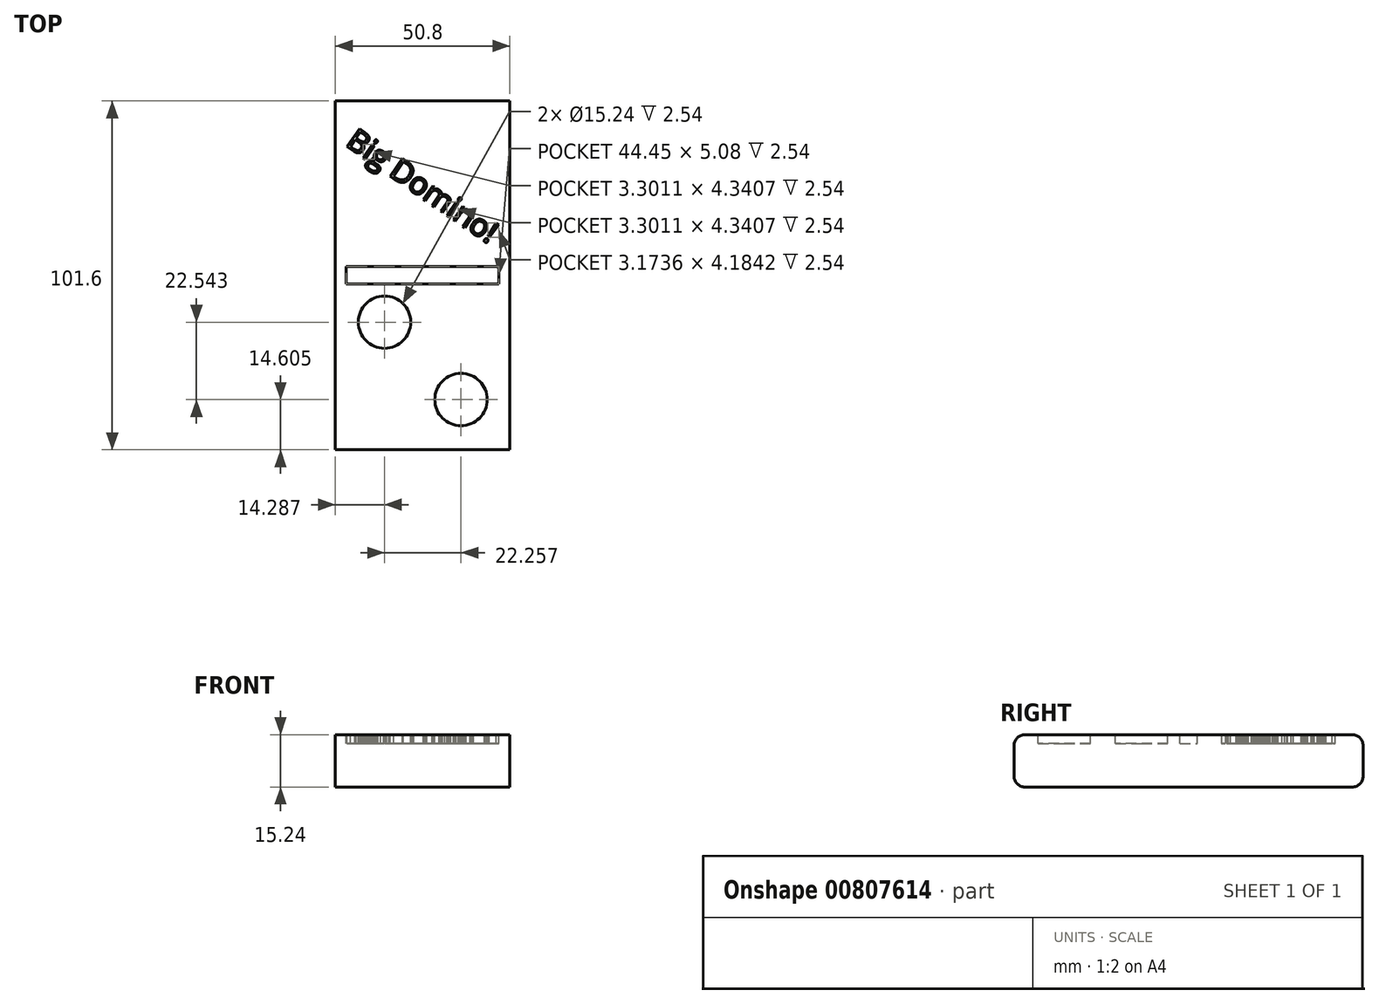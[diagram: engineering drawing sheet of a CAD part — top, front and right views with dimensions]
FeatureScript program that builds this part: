
annotation { "Feature Type Name" : "Feature", "Feature Type Description" : "" }
export const myFeature = defineFeature(function(context is Context, id is Id, definition is map)
    precondition{}
    {
        {
            var Q0;
            Q0=qCreatedBy(makeId("Top.planeOp"),FACE);
            var sketch = newSketch(context, id + "F0", { "sketchPlane" : qUnion([Q0])});
            skLineSegment(sketch, "E0.bottom", {"start": v(25.4, 50.8) * mm, "end": v(-25.4, 50.8) * mm});
            skLineSegment(sketch, "E0.top", {"start": v(25.4, -50.8) * mm, "end": v(-25.4, -50.8) * mm});
            skLineSegment(sketch, "E0.left", {"start": v(25.4, 50.8) * mm, "end": v(25.4, -50.8) * mm});
            skLineSegment(sketch, "E0.right", {"start": v(-25.4, 50.8) * mm, "end": v(-25.4, -50.8) * mm});
            skPoint(sketch, "E0.middle", {"position": v(0, 0) * mm});
            skSolve(sketch);
        }
        {
            var Q0;
            Q0=makeQuery(id+"F0.imprint","IMPRINT",FACE,{"disambiguationData":[TD([[makeQuery(id+"F0.imprint","IMPRINT",EDGE,{"derivedFrom":sQuery(id+"F0.wireOp",EDGE,"E0.bottom")}),1.0]])]});
            extrude(context, id + "F1", {"entities" : qUnion([Q0]), "depth" : 15.24 * mm, "offsetDistance" : 25.4 * mm});
        }
        {
            var Q0;
            Q0=makeQuery(id+"F1.opExtrude","CAP_EDGE",EDGE,{"disambiguationData":[OSD([sQuery(id+"F0.wireOp",EDGE,"E0.top")])],"isStart":false});
            var Q1;
            Q1=makeQuery(id+"F1.opExtrude","CAP_EDGE",EDGE,{"disambiguationData":[OSD([sQuery(id+"F0.wireOp",EDGE,"E0.top")])],"isStart":true});
            var Q2;
            Q2=makeQuery(id+"F1.opExtrude","CAP_EDGE",EDGE,{"disambiguationData":[OSD([sQuery(id+"F0.wireOp",EDGE,"E0.bottom")])],"isStart":false});
            var Q3;
            Q3=makeQuery(id+"F1.opExtrude","CAP_EDGE",EDGE,{"disambiguationData":[OSD([sQuery(id+"F0.wireOp",EDGE,"E0.bottom")])],"isStart":true});
            fillet(context, id + "F2", {"entities" : qUnion([Q0, Q1, Q2, Q3]), "radius" : 3.17 * mm, "tangentPropagation" : true, "allowEdgeOverflow" : false});
        }
        {
            var Q0;
            Q0=makeQuery(id+"F1.opExtrude","CAP_FACE",FACE,{"disambiguationData":[OSD([sQuery(id+"F0.wireOp",EDGE,"E0.bottom"),sQuery(id+"F0.wireOp",EDGE,"E0.top"),sQuery(id+"F0.wireOp",EDGE,"E0.left"),sQuery(id+"F0.wireOp",EDGE,"E0.right")])],"isStart":false});
            var sketch = newSketch(context, id + "F3", { "sketchPlane" : qUnion([Q0])});
            skLineSegment(sketch, "E1.bottom", {"start": v(22.23, -2.54) * mm, "end": v(-22.23, -2.54) * mm});
            skLineSegment(sketch, "E1.top", {"start": v(22.22, 2.54) * mm, "end": v(-22.23, 2.54) * mm});
            skLineSegment(sketch, "E1.left", {"start": v(22.22, -2.54) * mm, "end": v(22.22, 2.54) * mm});
            skLineSegment(sketch, "E1.right", {"start": v(-22.23, -2.54) * mm, "end": v(-22.23, 2.54) * mm});
            skPoint(sketch, "E1.middle", {"position": v(0, 0) * mm});
            skText(sketch, "E2", { "text": "Big Domino!", "fontName": "OpenSans-Regular.ttf"});
            skPoint(sketch, "E3", {"position": v(0, 26.17) * mm});
            skLineSegment(sketch, "E4.bottom", {"start": v(-22.23, -2.54) * mm, "end": v(0, -2.54) * mm, "construction": true});
            skLineSegment(sketch, "E4.top", {"start": v(-22.22, -24.77) * mm, "end": v(0, -24.77) * mm, "construction": true});
            skLineSegment(sketch, "E4.left", {"start": v(-22.23, -2.54) * mm, "end": v(-22.23, -24.77) * mm, "construction": true});
            skLineSegment(sketch, "E4.right", {"start": v(0, -2.54) * mm, "end": v(0, -24.77) * mm, "construction": true});
            skLineSegment(sketch, "E5.bottom", {"start": v(0, -24.77) * mm, "end": v(22.29, -24.77) * mm, "construction": true});
            skLineSegment(sketch, "E5.top", {"start": v(0, -47.63) * mm, "end": v(22.29, -47.63) * mm, "construction": true});
            skLineSegment(sketch, "E5.left", {"start": v(0, -24.77) * mm, "end": v(0, -47.63) * mm, "construction": true});
            skLineSegment(sketch, "E5.right", {"start": v(22.29, -24.77) * mm, "end": v(22.29, -47.62) * mm, "construction": true});
            skLineSegment(sketch, "E6", {"start": v(-22.23, -13.65) * mm, "end": v(0, -13.65) * mm, "construction": true});
            skLineSegment(sketch, "E7", {"start": v(0, -13.65) * mm, "end": v(22.29, -36.2) * mm, "construction": true});
            skLineSegment(sketch, "E8", {"start": v(22.29, -36.2) * mm, "end": v(0, -36.2) * mm, "construction": true});
            skPoint(sketch, "E9", {"position": v(-11.11, -13.65) * mm});
            skPoint(sketch, "E10", {"position": v(11.14, -36.2) * mm});
            skCircle(sketch, "E11", {"center": v(-11.11, -13.65) * mm, "radius": 7.62 * mm});
            skCircle(sketch, "E12", {"center": v(11.14, -36.2) * mm, "radius": 7.62 * mm});
            const initialGuessF3  = {"E2": [-0.02274, 0.03793, 0.82373, -0.56698, 0.00642]};
            skSetInitialGuess(sketch, initialGuessF3);
            skSolve(sketch);
        }
        {
            var Q0;
            Q0 = qSketchRegion(id + "F3", true);
            extrude(context, id + "F4", {"entities" : qUnion([Q0]), "operationType" : NewBodyOperationType.REMOVE, "oppositeDirection" : true, "depth" : 2.54 * mm, "offsetDistance" : 25.4 * mm});
        }
    });
